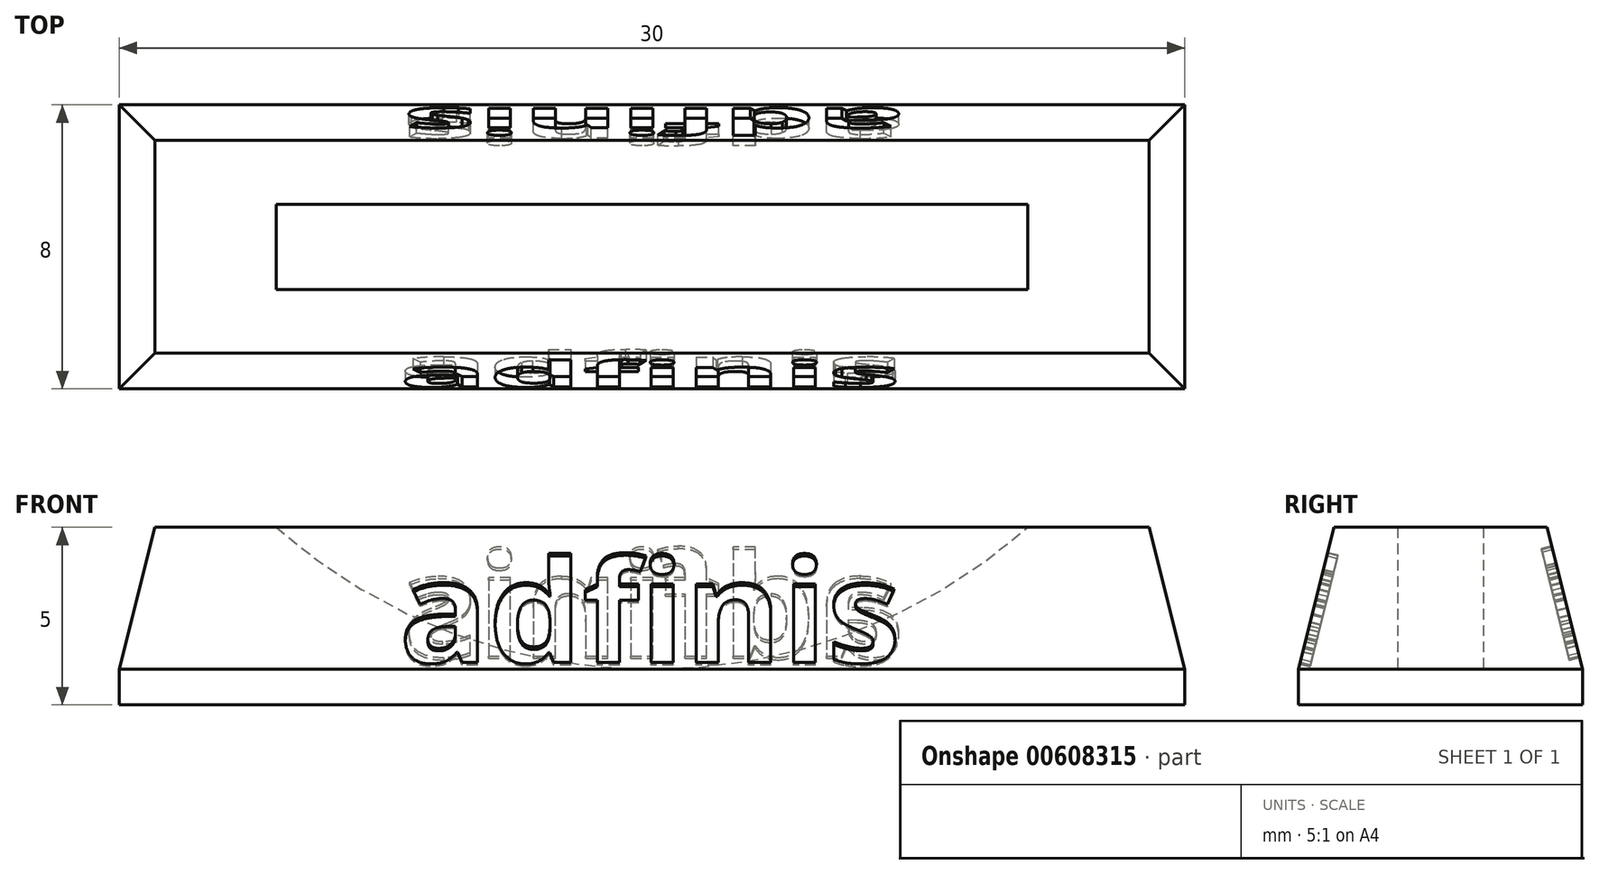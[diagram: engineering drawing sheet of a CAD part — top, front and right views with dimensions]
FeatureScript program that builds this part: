
annotation { "Feature Type Name" : "Feature", "Feature Type Description" : "" }
export const myFeature = defineFeature(function(context is Context, id is Id, definition is map)
    precondition{}
    {
        {
            var Q0;
            Q0=qCreatedBy(makeId("Top.planeOp"),FACE);
            var sketch = newSketch(context, id + "F0", { "sketchPlane" : qUnion([Q0])});
            skLineSegment(sketch, "E0.bottom", {"start": v(15, 2) * mm, "end": v(-15, 2) * mm});
            skLineSegment(sketch, "E0.top", {"start": v(15, -2) * mm, "end": v(-15, -2) * mm});
            skLineSegment(sketch, "E0.left", {"start": v(15, 2) * mm, "end": v(15, -2) * mm});
            skLineSegment(sketch, "E0.right", {"start": v(-15, 2) * mm, "end": v(-15, -2) * mm});
            skPoint(sketch, "E0.middle", {"position": v(0, 0) * mm});
            skSolve(sketch);
        }
        {
            var Q0;
            Q0=makeQuery(id+"F0.imprint","IMPRINT",FACE,{"disambiguationData":[TD([[makeQuery(id+"F0.imprint","IMPRINT",EDGE,{"derivedFrom":sQuery(id+"F0.wireOp",EDGE,"E0.bottom")}),1.0]])]});
            extrude(context, id + "F1", {"entities" : qUnion([Q0]), "depth" : 5 * mm, "offsetDistance" : 25 * mm});
        }
        {
            var Q0;
            Q0=makeQuery(id+"F1.opExtrude","CAP_EDGE",EDGE,{"disambiguationData":[OSD([sQuery(id+"F0.wireOp",EDGE,"E0.bottom")])],"isStart":false});
            var Q1;
            Q1=makeQuery(id+"F1.opExtrude","CAP_EDGE",EDGE,{"disambiguationData":[OSD([sQuery(id+"F0.wireOp",EDGE,"E0.right")])],"isStart":false});
            var Q2;
            Q2=makeQuery(id+"F1.opExtrude","CAP_EDGE",EDGE,{"disambiguationData":[OSD([sQuery(id+"F0.wireOp",EDGE,"E0.left")])],"isStart":false});
            chamfer(context, id + "F2", {"entities" : qUnion([Q0, Q1, Q2]), "chamferType" : ChamferType.TWO_OFFSETS, "width1" : 1 * mm, "oppositeDirection" : false, "width2" : 4 * mm, "tangentPropagation" : true});
        }
        {
            var Q0;
            Q0=makeQuery(id+"F1.opExtrude","SWEPT_FACE",FACE,{"disambiguationData":[OSD([sQuery(id+"F0.wireOp",EDGE,"E0.top")])]});
            var sketch = newSketch(context, id + "F3", { "sketchPlane" : qUnion([Q0])});
            skLineSegment(sketch, "E1", {"start": v(0, 0) * mm, "end": v(0, 21) * mm, "construction": true});
            skPoint(sketch, "E1.endSnap0", {"position": v(0, 5) * mm});
            skCircle(sketch, "E2", {"center": v(0, 17) * mm, "radius": 16 * mm});
            skLineSegment(sketch, "E3", {"start": v(15, 1) * mm, "end": v(-15, 1) * mm, "construction": true});
            skSolve(sketch);
        }
        {
            var Q0;
            {var subQ0=sQuery(id+"F3.wireOp",EDGE,"E2");var subQ1=makeQuery(id+"F1.opExtrude","CAP_EDGE",EDGE,{"disambiguationData":[OSD([sQuery(id+"F0.wireOp",EDGE,"E0.top")])],"isStart":false});var subQ2=makeQuery(id+"F3.imprint","INTERSECT",VERTEX,{"disambiguationData":[OD(0.0)],"derivedFrom":[subQ1,subQ0]});Q0=makeQuery(id+"F3.imprint","IMPRINT",FACE,{"disambiguationData":[TD([[makeQuery(id+"F3.imprint","IMPRINT",EDGE,{"disambiguationData":[TD([[subQ2,1.0]])],"derivedFrom":subQ0}),1.0]])]});}
            extrude(context, id + "F4", {"entities" : qUnion([Q0]), "operationType" : NewBodyOperationType.REMOVE, "oppositeDirection" : true, "depth" : 1.2 * mm, "offsetDistance" : 25 * mm});
        }
        {
            var Q0;
            Q0=makeQuery(id+"F1.opExtrude","SWEPT_BODY",BODY,{"disambiguationData":[OSD([sQuery(id+"F0.wireOp",EDGE,"E0.bottom"),sQuery(id+"F0.wireOp",EDGE,"E0.top"),sQuery(id+"F0.wireOp",EDGE,"E0.left"),sQuery(id+"F0.wireOp",EDGE,"E0.right")])]});
            var Q1;
            Q1=makeQuery(id+"F1.opExtrude","SWEPT_FACE",FACE,{"disambiguationData":[OSD([sQuery(id+"F0.wireOp",EDGE,"E0.top")])]});
            mirror(context, id + "F5", {"operationType" : NewBodyOperationType.ADD, "entities" : qUnion([Q0]), "mirrorPlane" : qUnion([Q1])});
        }
        {
            var Q0;
            Q0=makeQuery(id+"F2.opChamfer","BLEND_FACE",FACE,{"disambiguationData":[OSD([sQuery(id+"F0.wireOp",EDGE,"E0.bottom")])]});
            var sketch = newSketch(context, id + "F6", { "sketchPlane" : qUnion([Q0])});
            skLineSegment(sketch, "E4", {"start": v(0, 0.49) * mm, "end": v(0, 4.6) * mm, "construction": true});
            skText(sketch, "E5", { "text": "adfinis", "fontName": "OpenSans-Bold.ttf"});
            const initialGuessF6  = {"E5": [-0.00712, 0.00087, 1, 0, 0.003]};
            skSetInitialGuess(sketch, initialGuessF6);
            skSolve(sketch);
        }
        {
            var Q0;
            Q0 = qSketchRegion(id + "F6", true);
            extrude(context, id + "F7", {"entities" : qUnion([Q0]), "operationType" : NewBodyOperationType.REMOVE, "oppositeDirection" : true, "depth" : .3 * mm, "offsetDistance" : 25 * mm});
        }
        {
            var Q0;
            Q0=makeQuery(id+"F5.opPattern","COPY",FACE,{"derivedFrom":makeQuery(id+"F2.opChamfer","BLEND_FACE",FACE,{"disambiguationData":[OSD([sQuery(id+"F0.wireOp",EDGE,"E0.bottom")])]}),"instanceName":"1"});
            var sketch = newSketch(context, id + "F8", { "sketchPlane" : qUnion([Q0])});
            skLineSegment(sketch, "E6", {"start": v(-14, 3.64) * mm, "end": v(14, 3.64) * mm, "construction": true});
            skText(sketch, "E7", { "text": "adfinis", "fontName": "OpenSans-Bold.ttf"});
            skLineSegment(sketch, "E8", {"start": v(0, 3.64) * mm, "end": v(0, -0.49) * mm, "construction": true});
            const initialGuessF8  = {"E7": [-0.00712, -0.00029, 1, 0, 0.003]};
            skSetInitialGuess(sketch, initialGuessF8);
            skSolve(sketch);
        }
        {
            var Q0;
            Q0 = qSketchRegion(id + "F8", true);
            extrude(context, id + "F9", {"entities" : qUnion([Q0]), "operationType" : NewBodyOperationType.REMOVE, "oppositeDirection" : true, "depth" : .3 * mm, "offsetDistance" : 25 * mm});
        }
    });
